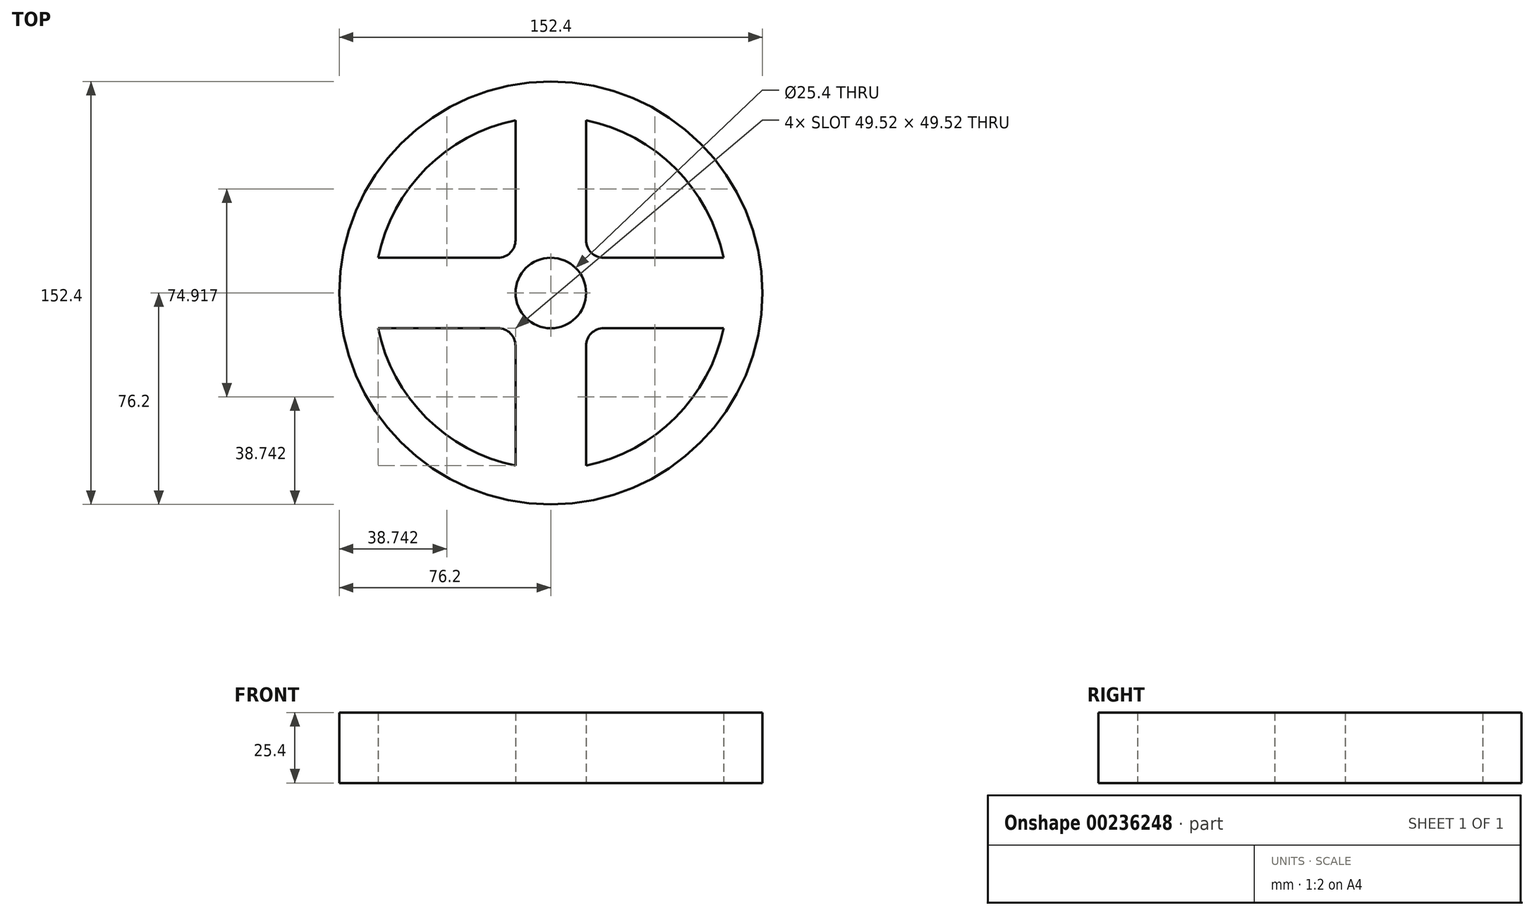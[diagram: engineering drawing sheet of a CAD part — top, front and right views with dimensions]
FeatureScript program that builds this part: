
annotation { "Feature Type Name" : "Feature", "Feature Type Description" : "" }
export const myFeature = defineFeature(function(context is Context, id is Id, definition is map)
    precondition{}
    {
        {
            var Q0;
            Q0=qCreatedBy(makeId("Top.planeOp"),FACE);
            var sketch = newSketch(context, id + "F0", { "sketchPlane" : qUnion([Q0])});
            skCircle(sketch, "E0", {"center": v(0, 0) * mm, "radius": 76.2 * mm});
            skArc(sketch, "E1", {"start": v(62.22, 12.7) * mm, "mid": v(44.9, 44.9) * mm, "end": v(12.7, 62.22) * mm});
            skCircle(sketch, "E2", {"center": v(0, 0) * mm, "radius": 12.7 * mm});
            skLineSegment(sketch, "E3", {"start": v(0, 0) * mm, "end": v(0, 63.5) * mm});
            skLineSegment(sketch, "E4.0", {"start": v(-12.7, 19.05) * mm, "end": v(-12.7, 62.22) * mm});
            skLineSegment(sketch, "E5.0", {"start": v(12.7, 19.05) * mm, "end": v(12.7, 62.22) * mm});
            skLineSegment(sketch, "E6", {"start": v(0, 0) * mm, "end": v(0, -63.5) * mm});
            skLineSegment(sketch, "E7.0", {"start": v(-12.7, -19.05) * mm, "end": v(-12.7, -62.22) * mm});
            skLineSegment(sketch, "E8.0", {"start": v(12.7, -19.05) * mm, "end": v(12.7, -62.22) * mm});
            skLineSegment(sketch, "E9", {"start": v(0, 0) * mm, "end": v(-63.5, 0) * mm});
            skLineSegment(sketch, "E10", {"start": v(0, 0) * mm, "end": v(63.5, 0) * mm});
            skLineSegment(sketch, "E11.0", {"start": v(-19.05, 12.7) * mm, "end": v(-62.22, 12.7) * mm});
            skLineSegment(sketch, "E12.0", {"start": v(-19.05, -12.7) * mm, "end": v(-62.22, -12.7) * mm});
            skLineSegment(sketch, "E13.0", {"start": v(19.05, -12.7) * mm, "end": v(62.22, -12.7) * mm});
            skLineSegment(sketch, "E14.0", {"start": v(19.05, 12.7) * mm, "end": v(62.22, 12.7) * mm});
            skLineSegment(sketch, "E15.trimOffspring", {"start": v(75.13, 12.7) * mm, "end": v(76.2, 12.7) * mm});
            skLineSegment(sketch, "E16.trimOffspring", {"start": v(75.13, -12.7) * mm, "end": v(76.2, -12.7) * mm});
            skLineSegment(sketch, "E17.trimOffspring", {"start": v(-75.13, -12.7) * mm, "end": v(-76.2, -12.7) * mm});
            skLineSegment(sketch, "E18.trimOffspring", {"start": v(-75.13, 12.7) * mm, "end": v(-76.2, 12.7) * mm});
            skLineSegment(sketch, "E19.trimOffspring", {"start": v(-12.7, 75.13) * mm, "end": v(-12.7, 76.2) * mm});
            skLineSegment(sketch, "E20.trimOffspring", {"start": v(12.7, 75.13) * mm, "end": v(12.7, 76.2) * mm});
            skLineSegment(sketch, "E21.trimOffspring", {"start": v(12.7, -75.13) * mm, "end": v(12.7, -76.2) * mm});
            skLineSegment(sketch, "E22.trimOffspring", {"start": v(-12.7, -75.13) * mm, "end": v(-12.7, -76.05) * mm});
            skArc(sketch, "E23.trimOffspring", {"start": v(12.7, -62.22) * mm, "mid": v(44.9, -44.9) * mm, "end": v(62.22, -12.7) * mm});
            skArc(sketch, "E24.trimOffspring", {"start": v(-62.22, -12.7) * mm, "mid": v(-44.9, -44.9) * mm, "end": v(-12.7, -62.22) * mm});
            skArc(sketch, "E25.trimOffspring", {"start": v(-12.7, 62.22) * mm, "mid": v(-44.9, 44.9) * mm, "end": v(-62.22, 12.7) * mm});
            skPoint(sketch, "E26.visualSharp", {"position": v(-12.7, 12.7) * mm});
            skArc(sketch, "E26.filletArc", {"start": v(-19.05, 12.7) * mm, "mid": v(-14.56, 14.56) * mm, "end": v(-12.7, 19.05) * mm});
            skPoint(sketch, "E27.visualSharp", {"position": v(12.7, 12.7) * mm});
            skArc(sketch, "E27.filletArc", {"start": v(12.7, 19.05) * mm, "mid": v(14.56, 14.56) * mm, "end": v(19.05, 12.7) * mm});
            skPoint(sketch, "E28.visualSharp", {"position": v(-12.7, -12.7) * mm});
            skArc(sketch, "E28.filletArc", {"start": v(-12.7, -19.05) * mm, "mid": v(-14.56, -14.56) * mm, "end": v(-19.05, -12.7) * mm});
            skPoint(sketch, "E29.visualSharp", {"position": v(12.7, -12.7) * mm});
            skArc(sketch, "E29.filletArc", {"start": v(19.05, -12.7) * mm, "mid": v(14.56, -14.56) * mm, "end": v(12.7, -19.05) * mm});
            skSolve(sketch);
        }
        {
            var Q0;
            Q0 = qSketchRegion(id + "F0", true);
            extrude(context, id + "F1", {"entities" : qUnion([Q0]), "endBound" : BoundingType.SYMMETRIC, "depth" : 25.4 * mm});
        }
    });
